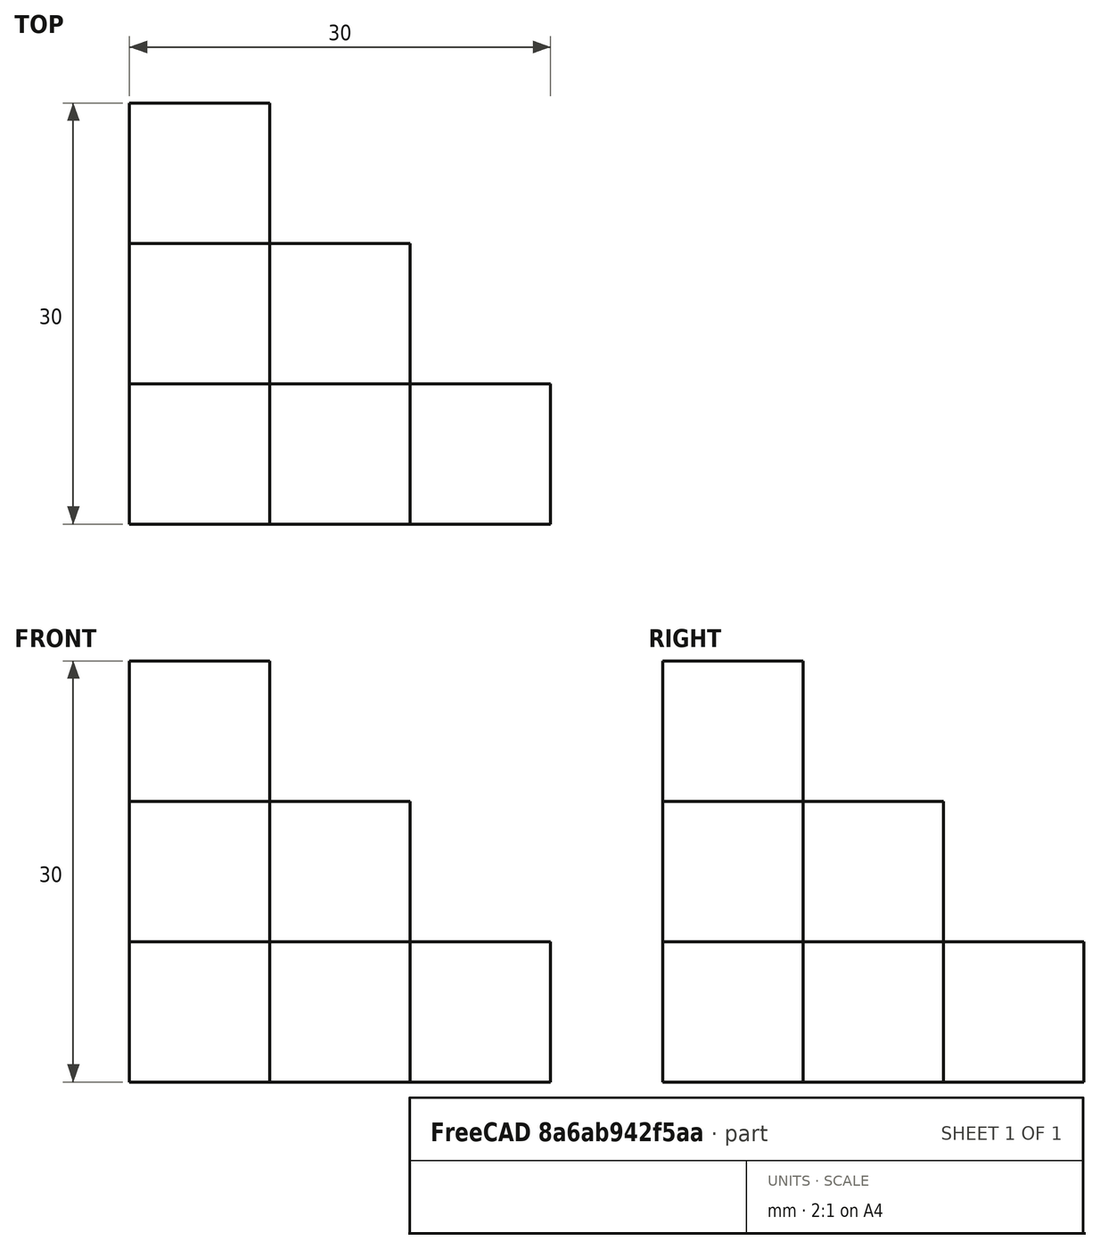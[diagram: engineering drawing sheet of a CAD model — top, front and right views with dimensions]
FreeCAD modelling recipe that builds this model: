
FCSTD DOCUMENT  (FreeCAD 1.0R39319 (Git))
Label: oft1_t04r01_qbert 3 levels
License: All rights reserved
LicenseURL: https://en.wikipedia.org/wiki/All_rights_reserved
objects: Part::Box×6
note: 6 computed .brp shape members not serialized (recipe doc carries the construction recipe); baked Part::Feature solids carry a one-line shape summary decoded from their .brp

FEATURE [Part::Box] Box  label="cubo-1"
  AttacherType = Attacher::AttachEngine3D
  Height = 10
  Length = 10
  Placement = pos=(0,0,10) rot=(0,0,1;0rad)
  Width = 10
FEATURE [Part::Box] Box001  label="cubo-2"
  AttacherType = Attacher::AttachEngine3D
  Height = 10
  Length = 10
  Placement = pos=(10,0,0) rot=(0,0,1;0rad)
  Width = 10
FEATURE [Part::Box] Box002  label="Cub"
  AttacherType = Attacher::AttachEngine3D
  Height = 10
  Length = 10
  Placement = pos=(0,10,0) rot=(0,0,1;0rad)
  Width = 10
FEATURE [Part::Box] Box003  label="Cub001"
  AttacherType = Attacher::AttachEngine3D
  Height = 10
  Length = 10
  Placement = pos=(-10,10,10) rot=(0,0,1;0rad)
  Width = 10
FEATURE [Part::Box] Box004  label="Cub002"
  AttacherType = Attacher::AttachEngine3D
  Height = 10
  Length = 10
  Placement = pos=(-10,20,0) rot=(0,0,1;0rad)
  Width = 10
FEATURE [Part::Box] Box005  label="Cub003"
  AttacherType = Attacher::AttachEngine3D
  Height = 10
  Length = 10
  Placement = pos=(-10,0,20) rot=(0,0,1;0rad)
  Width = 10
